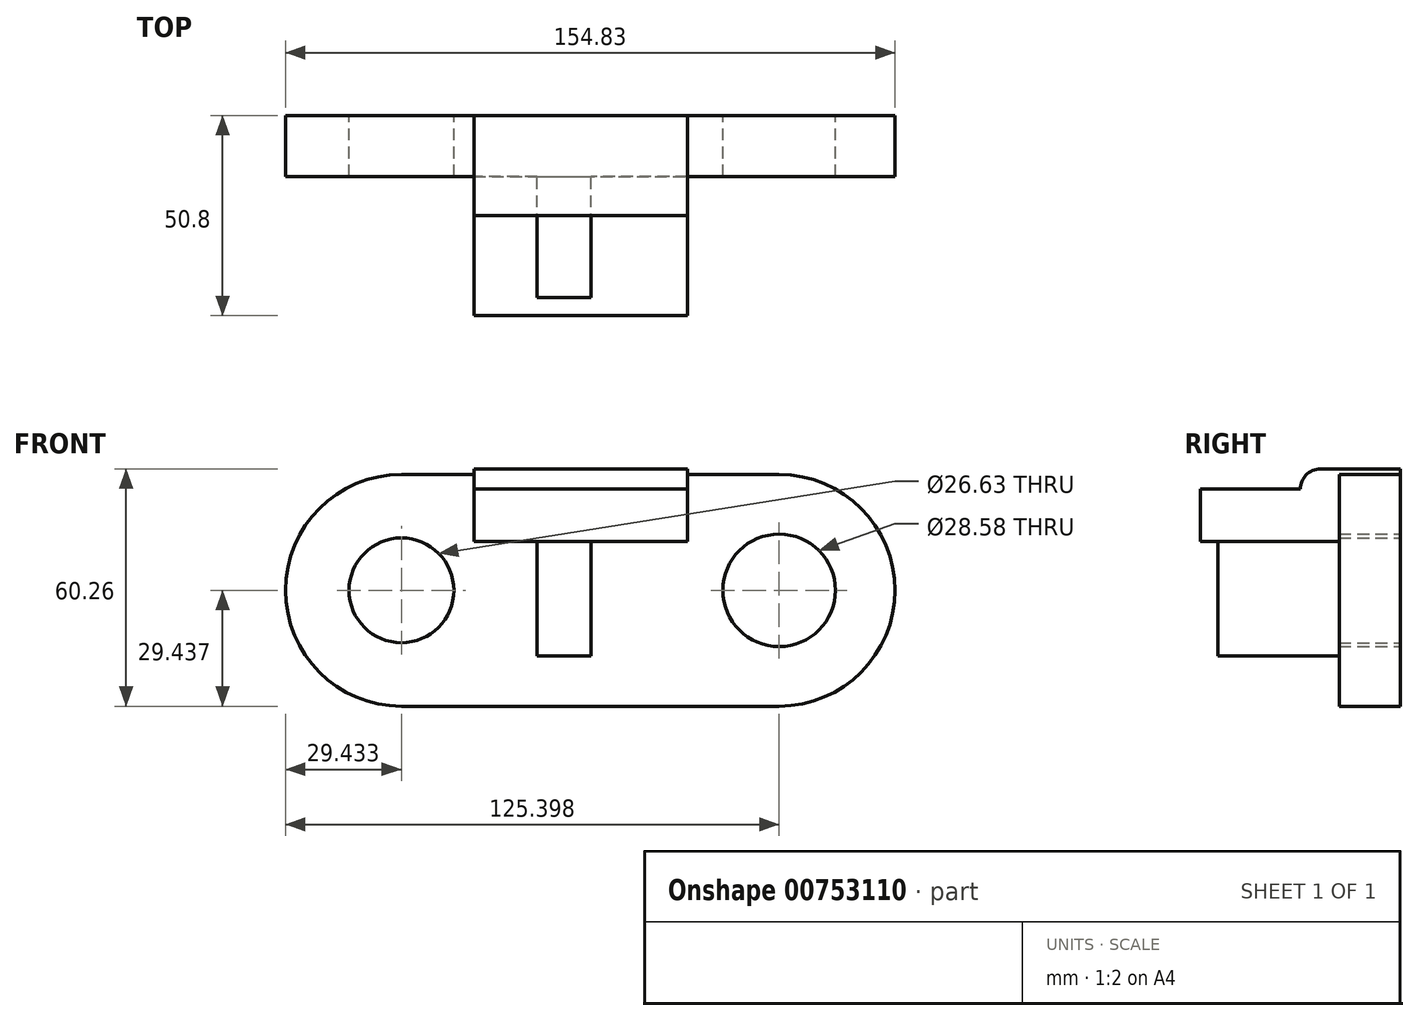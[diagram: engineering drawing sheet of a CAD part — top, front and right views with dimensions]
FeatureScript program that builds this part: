
annotation { "Feature Type Name" : "Feature", "Feature Type Description" : "" }
export const myFeature = defineFeature(function(context is Context, id is Id, definition is map)
    precondition{}
    {
        {
            var Q0;
            Q0=qCreatedBy(makeId("Front.planeOp"),FACE);
            var sketch = newSketch(context, id + "F0", { "sketchPlane" : qUnion([Q0])});
            skLineSegment(sketch, "E0.bottom", {"start": v(-48.23, 29.45) * mm, "end": v(47.74, 29.45) * mm});
            skLineSegment(sketch, "E0.top", {"start": v(-48.23, -29.42) * mm, "end": v(47.74, -29.42) * mm});
            skArc(sketch, "E1", {"start": v(-48.23, 29.45) * mm, "mid": v(-77.66, 0.02) * mm, "end": v(-48.23, -29.42) * mm});
            skArc(sketch, "E2", {"start": v(47.74, -29.42) * mm, "mid": v(77.17, 0.02) * mm, "end": v(47.74, 29.45) * mm});
            skCircle(sketch, "E3", {"center": v(-48.23, 0.02) * mm, "radius": 13.31 * mm});
            skCircle(sketch, "E4", {"center": v(47.74, 0.02) * mm, "radius": 14.3 * mm});
            skSolve(sketch);
        }
        {
            var Q0;
            Q0=makeQuery(id+"F0.imprint","IMPRINT",FACE,{"disambiguationData":[TD([[makeQuery(id+"F0.imprint","IMPRINT",EDGE,{"derivedFrom":sQuery(id+"F0.wireOp",EDGE,"E0.bottom")}),-1.0]])]});
            extrude(context, id + "F1", {"entities" : qUnion([Q0]), "depth" : 15.48 * mm, "offsetDistance" : 25.4 * mm});
        }
        {
            var Q0;
            Q0=qCreatedBy(makeId("Front.planeOp"),FACE);
            var sketch = newSketch(context, id + "F2", { "sketchPlane" : qUnion([Q0])});
            skLineSegment(sketch, "E5.bottom", {"start": v(-29.83, 30.84) * mm, "end": v(24.43, 30.84) * mm});
            skLineSegment(sketch, "E5.top", {"start": v(-29.83, 12.42) * mm, "end": v(24.43, 12.42) * mm});
            skLineSegment(sketch, "E5.left", {"start": v(-29.83, 30.84) * mm, "end": v(-29.83, 12.42) * mm});
            skLineSegment(sketch, "E5.right", {"start": v(24.43, 30.84) * mm, "end": v(24.43, 12.42) * mm});
            skSolve(sketch);
        }
        {
            var Q0;
            Q0=makeQuery(id+"F2.imprint","IMPRINT",FACE,{"disambiguationData":[TD([[makeQuery(id+"F2.imprint","IMPRINT",EDGE,{"derivedFrom":sQuery(id+"F2.wireOp",EDGE,"E5.bottom")}),-1.0]])]});
            extrude(context, id + "F3", {"entities" : qUnion([Q0]), "operationType" : NewBodyOperationType.ADD, "depth" : 25.4 * mm, "offsetDistance" : 25.4 * mm});
        }
        {
            var Q0;
            Q0=makeQuery(id+"F3.opExtrude","CAP_EDGE",EDGE,{"disambiguationData":[OSD([sQuery(id+"F2.wireOp",EDGE,"E5.bottom")])],"isStart":false});
            fillet(context, id + "F4", {"entities" : qUnion([Q0]), "radius" : 5.08 * mm, "tangentPropagation" : true, "allowEdgeOverflow" : false});
        }
        {
            var Q0;
            Q0=makeQuery(id+"F3.opExtrude","CAP_FACE",FACE,{"disambiguationData":[OSD([sQuery(id+"F2.wireOp",EDGE,"E5.bottom"),sQuery(id+"F2.wireOp",EDGE,"E5.top"),sQuery(id+"F2.wireOp",EDGE,"E5.left"),sQuery(id+"F2.wireOp",EDGE,"E5.right")])],"isStart":false});
            extrude(context, id + "F5", {"entities" : qUnion([Q0]), "operationType" : NewBodyOperationType.ADD, "depth" : 25.4 * mm, "offsetDistance" : 25.4 * mm});
        }
        {
            var Q0;
            Q0=qCreatedBy(makeId("Right.planeOp"),FACE);
            var sketch = newSketch(context, id + "F6", { "sketchPlane" : qUnion([Q0])});
            skLineSegment(sketch, "E6.bottom", {"start": v(-46.27, 25.82) * mm, "end": v(0, 25.82) * mm});
            skLineSegment(sketch, "E6.top", {"start": v(-46.27, -16.6) * mm, "end": v(0, -16.6) * mm});
            skLineSegment(sketch, "E6.left", {"start": v(-46.27, 25.82) * mm, "end": v(-46.27, -16.6) * mm});
            skLineSegment(sketch, "E6.right", {"start": v(0, 25.82) * mm, "end": v(0, -16.6) * mm});
            skSolve(sketch);
        }
        {
            var Q0;
            Q0=makeQuery(id+"F6.imprint","IMPRINT",FACE,{"disambiguationData":[TD([[makeQuery(id+"F6.imprint","IMPRINT",EDGE,{"derivedFrom":sQuery(id+"F6.wireOp",EDGE,"E6.bottom")}),-1.0]])]});
            extrude(context, id + "F7", {"entities" : qUnion([Q0]), "operationType" : NewBodyOperationType.ADD, "oppositeDirection" : true, "depth" : 13.8 * mm, "offsetDistance" : 25.4 * mm});
        }
        {
            var Q0;
            Q0=qCreatedBy(makeId("Top.planeOp"),FACE);
            var sketch = newSketch(context, id + "F8", { "sketchPlane" : qUnion([Q0])});
            skLineSegment(sketch, "E7.bottom", {"start": v(-28.84, -42.1) * mm, "end": v(23.7, -42.1) * mm});
            skLineSegment(sketch, "E7.top", {"start": v(-28.84, -54.87) * mm, "end": v(23.7, -54.87) * mm});
            skLineSegment(sketch, "E7.left", {"start": v(-28.84, -42.1) * mm, "end": v(-28.84, -54.87) * mm});
            skLineSegment(sketch, "E7.right", {"start": v(23.7, -42.1) * mm, "end": v(23.7, -54.87) * mm});
            skSolve(sketch);
        }
        {
            var Q0;
            Q0=sQuery(id+"F8.wireOp",EDGE,"E7.bottom");
            var Q1;
            Q1=sQuery(id+"F8.wireOp",EDGE,"E7.top");
            extrude(context, id + "F9", {"bodyType" : ToolBodyType.SURFACE, "surfaceEntities" : qUnion([Q0, Q1]), "depth" : 25.4 * mm, "offsetDistance" : 25.4 * mm});
        }
    });
